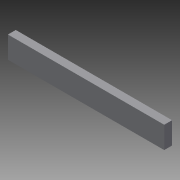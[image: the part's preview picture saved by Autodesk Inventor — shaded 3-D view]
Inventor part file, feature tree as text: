
AUTODESK INVENTOR PART (.ipt)
format: ipt  version: 2013 (Build 170138000, 138)  size: 115,200 bytes
history: native  units: mm
features: extrude x6, sketch x6, other x1
ambient origin geometry x8: Origin, YZ Plane, XZ Plane, XY Plane, X Axis, Y Axis, Z Axis, Center Point
feature tree (13):
  other  "ソリッド1"
  extrude  "押し出し1"  Depth=90.0mm
  extrude  "押し出し2"  Depth=10.0mm
  extrude  "押し出し3"  Depth=0.5mm TaperAngle=0.0deg
  extrude  "押し出し4"  Depth=5.0mm
  extrude  "押し出し5"  Depth=5.0mm TaperAngle=0.0deg
  extrude  "押し出し6"  Depth=5.0mm TaperAngle=0.0deg
  sketch  "スケッチ1"
  sketch  "スケッチ2"
  sketch  "スケッチ3"
  sketch  "スケッチ4"
  sketch  "スケッチ5"
  sketch  "スケッチ6"
